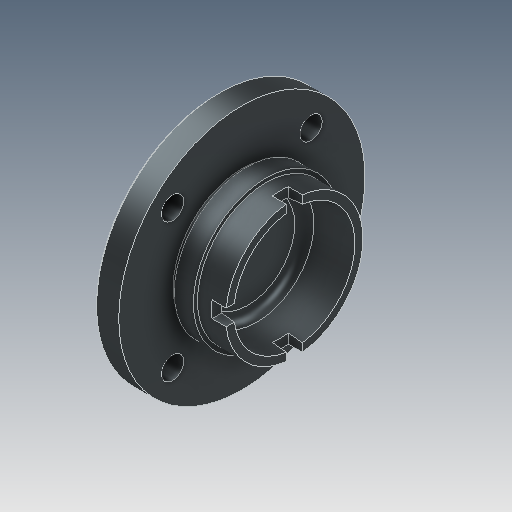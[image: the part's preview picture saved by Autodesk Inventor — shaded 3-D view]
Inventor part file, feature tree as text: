
AUTODESK INVENTOR PART (.ipt)
format: ipt  version: 2025 (Build 290162000, 162)  size: 220,160 bytes
history: native  units: in
note: dims shown in document units (in); Inventor stores cm internally (conversion verified against a paired STEP export)
features: sketch x5, extrude x3, revolve x1, chamfer x1, fillet x1
ambient origin geometry x8: Origin, YZ Plane, XZ Plane, XY Plane, X Axis, Y Axis, Z Axis, Center Point
bodies: 实体1 (feature_tree)
feature tree (11):
  revolve  "旋转1"  [1 undecoded]
  extrude  "拉伸1"  Depth=0.4724in
  extrude  "拉伸2"  Depth=1.3386in
  extrude  "拉伸3"  Depth=0.0984in
  chamfer  "倒角1"  Angle=45.0deg  [1 undecoded]
  fillet  "圆角1"  Radius=0.0394in
  sketch  "草图1"  dims[d3=0.3937in d0=0.4331in d1=1.0236in d2=2.4016in]
  sketch  "草图2"  dims[d6=1.4173in d7=1.3386in]
  sketch  "草图3"  dims[d8=0.4724in d9=0.0984in]
  sketch  "草图4"  dims[d10=1.3386in d11=45.0deg d12=0.0394in d13=0.5906in d14=1.1811in d15=0.5792in d16=90.0deg d17=0.2756in d18=0.315in d19=0.0in d20=0.2756in d21=0.315in d22=0.0in d23=0.4331in d24=1.9094in d25=1.5748in d27=360.0deg d29=0.315in d30=0.0in d31=0.0394in d32=0.0787in d33=45.0deg d34=0.1969in d35=45.0deg]
  sketch  "草图 - 环形阵列1"  dims[d4=1.0236in d5=0.4724in]
note: 2 required parameter values undecoded (feature->parameter linkage not recoverable at this tier; creation-order binding heuristic only, values carry confidence <= 0.55)